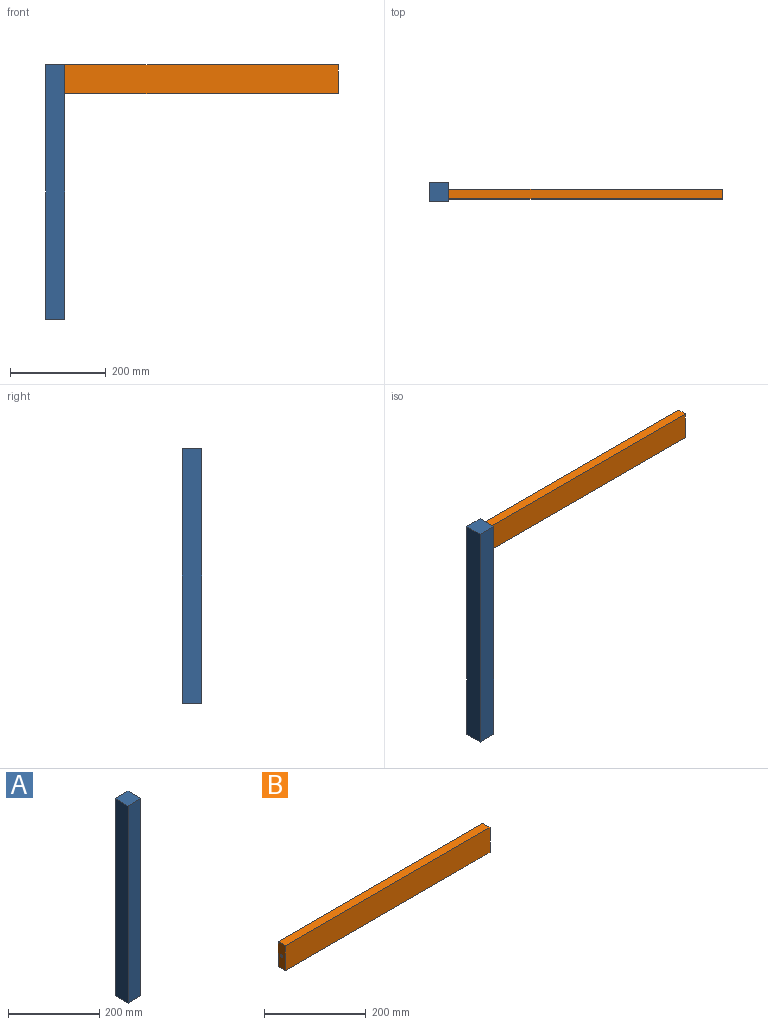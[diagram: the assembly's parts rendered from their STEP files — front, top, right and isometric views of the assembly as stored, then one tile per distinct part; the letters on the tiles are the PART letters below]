
ASSEMBLY  parts=2 mates=1
PART A: 12 faces, bbox 40x40x530 mm
  f0: plane 530x40mm, normal (1,0,0), area 21143.5mm2, adj f1,f3,f4,f5,f6,f10
  f1: plane 530x40mm, normal (0,1,0), area 21171.7mm2, adj f0,f2,f4,f5,f8
  f2: plane 530x40mm, normal (-1,0,0), area 21200mm2, adj f1,f3,f4,f5
  f3: plane 530x40mm, normal (0,-1,0), area 21200mm2, adj f0,f2,f4,f5
  f4: plane 40x40mm, normal (0,0,1), area 1600mm2, adj f0,f1,f2,f3
  f5: plane 40x40mm, normal (0,0,-1), area 1600mm2, adj f0,f1,f2,f3
  f6: cylinder r=3mm len=12mm, axis (1,0,0), area 226.2mm2, adj f0,f7
  f7: plane 6x6mm, normal (1,0,0), area 28.3mm2, adj f6
  f8: cylinder r=3mm len=12mm, axis (0,1,0), area 226.2mm2, adj f1,f9
  f9: plane 6x6mm, normal (0,1,0), area 28.3mm2, adj f8
  f10: cylinder r=3mm len=12mm, axis (1,0,0), area 226.2mm2, adj f0,f11
  f11: plane 6x6mm, normal (1,0,0), area 28.3mm2, adj f10
PART B: 10 faces, bbox 570x20x60 mm
  f0: plane 570x60mm, normal (0,1,0), area 34200mm2, adj f1,f3,f4,f5
  f1: plane 570x20mm, normal (0,0,1), area 11400mm2, adj f0,f2,f4,f5
  f2: plane 570x60mm, normal (0,-1,0), area 34200mm2, adj f1,f3,f4,f5
  f3: plane 570x20mm, normal (0,0,-1), area 11400mm2, adj f0,f2,f4,f5
  f4: plane 60x20mm, normal (1,0,0), area 1171.7mm2, adj f0,f1,f2,f3,f6
  f5: plane 60x20mm, normal (-1,0,0), area 1171.7mm2, adj f0,f1,f2,f3,f8
  f6: cylinder r=3mm len=12mm, axis (1,0,0), area 226.2mm2, adj f4,f7
  f7: plane 6x6mm, normal (1,0,0), area 28.3mm2, adj f6
  f8: cylinder r=3mm len=12mm, axis (-1,0,0), area 226.2mm2, adj f5,f9
  f9: plane 6x6mm, normal (-1,0,0), area 28.3mm2, adj f8
PLACE A t=(-414.22,-231.67,11.23)mm fixed
PLACE B t=(-109.22,-236.67,246.23)mm
MATE fastened B.f6 <-> A.f6  axis (-1,0,0) through (-394.22,-236.67,246.23)mm
